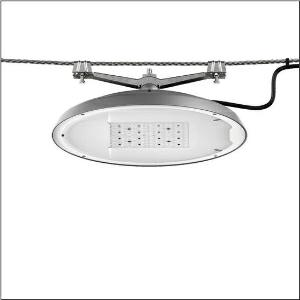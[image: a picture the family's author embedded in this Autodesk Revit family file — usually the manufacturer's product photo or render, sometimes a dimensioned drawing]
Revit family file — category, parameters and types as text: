
# Revit family: dl_r__50_iq_mini___st1_0s_5xa248w31f08le_ba39
name_source: partatom
category: Lighting Fixtures
units: mm (PartAtom-declared; Revit-internal decimal feet)

## family parameters
Cut with Voids When Loaded = No
Host = Face
Light Source = No
Part Type = Normal
Room Calculation Point = No
Round Connector Dimension = Use Diameter
Shared = No

## types (1)
- --- (1 x LED, 10390 lm, 67.4 W, 3000K)
    Apparent Load = 67 VA
    CIE Flux Codes = 37 72 97 100 100
    Color Rendering = 70
    Color Temperature = 3000K
    Default Elevation = 1800 mm
    Description = DL® 50 iQ mini, catenary luminaire, primary light control with lens, of PMMA, primary optical cover: cover, of toughened safety glass, transparent, light distribution: ST1.0s, light emission: direct distribution, primary light characteristic: symmetric, installation type: suspended mounting, LED, High Power LED, rated luminous flux: 10.390lm, luminous efficacy: 154lm/W, light colour: 730, colour temperature: 3000K, control: optimised constant luminous flux control (CLO 2.0), Desk-Remote (wireless, voltage-free reading and setting of iQ features in the workshop via application-optimized NFC function/RFID function), Light-Fading, Smart-Wire, Night-Set, Lumen-Switch, Temp-Guard, Auto-Match, Street-Remote, mains connection: 230..240V, AC, 50/60Hz, start of lifetime: 67W, end of service life: 70W, reduction: 31W, luminaire housing, of diecast aluminium, powder-coated, Siteco® metallic grey (DB 702S), diameter: 500mm, height: 115mm, protection rating (complete): IP66, insulation class (complete): insulation class II (safety insulation), certification: CE, ENEC, ENEC+, VDE, impact resistance: IK08, permissible operating ambient temperature for outdoor applications: -25..+40°C, standard-compliant lighting for roads and squares, packaging unit: 1 piece

Light Distribution: ST1.0s
    Height = 124 mm  [stored 0.406824 ft]
    Lamp = 1 x LED
    Lamp Light Flux = 10390 lm
    Lamp Power = 67.4 W
    Lamp count = 1
    Length = 500 mm
    Luminous efficacy = 154 lm/W
    Manufacturer = Siteco
    ModVariant = No
    Model = 5XA248W31F08LE
    Number of Poles = 1
    OnlyDefault = Yes
    Power Factor = 1
    Product Name = DL® 50 iQ mini | ST1.0s
    Product group = catenary luminaire
    ProductGroupID = 6300
    Protection Class = Protection class II
    Protection Degree = IP 66
    RLX_Detail_Level = 1
    RLX_Emergency_Light_Flux = 0 lm
    RLX_Emergency_Type = 0
    RLX_Emergency_Type_DB = No
    RlxData = <blob elided: 126685 chars, md5=4aa24d80>
    Socket = socket
    Standby Power = 0 W
    System Light Flux = 10390 lm
    System Power = 67 W
    Type Comments = factory setting: luminous flux: 100 % | dim-lin: 254 | 705 mA
    Type Image = l_1251783.jpg
    URL = http://relux.com
    VarID = @adj_110329
    Voltage = 0 V
    Weight = 0.00 kg
    Width = 0 mm  [stored 0 ft]

note: [stored X ft] marks values corroborated as IEEE doubles in the binary element streams (Revit-internal decimal feet)

## geometry (parser evidence)
native form markers: Blend x4, Sweep x12
no freeform markers — native parametric forms only
